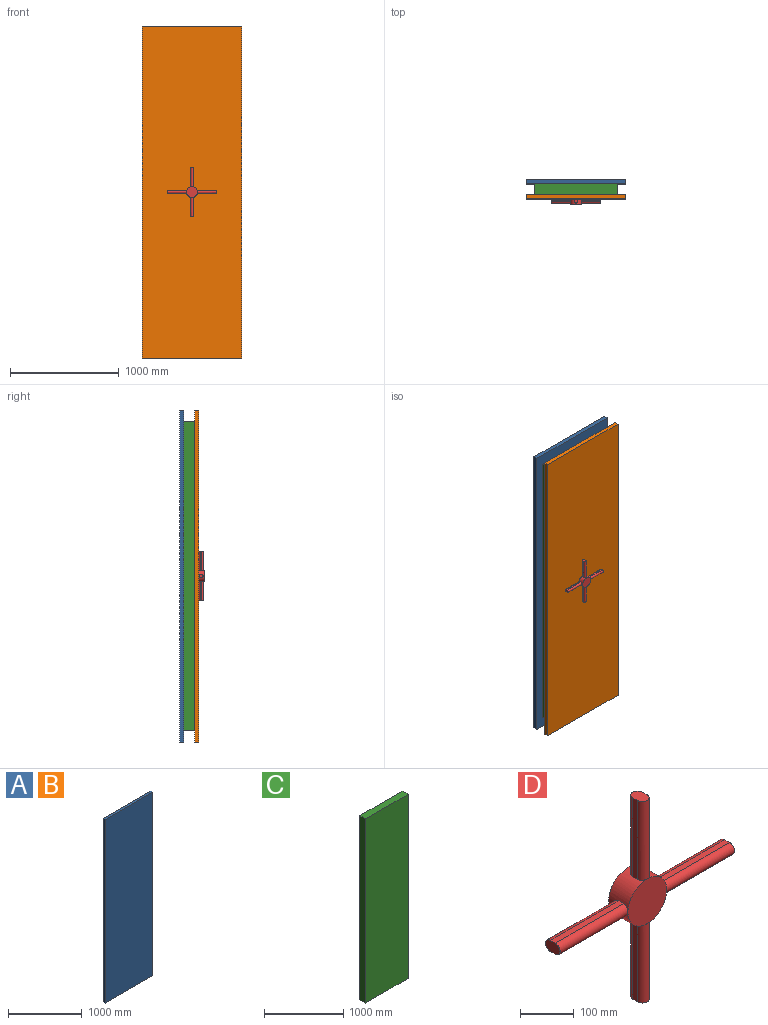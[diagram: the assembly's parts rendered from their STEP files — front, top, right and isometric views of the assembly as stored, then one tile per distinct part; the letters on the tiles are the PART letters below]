
ASSEMBLY  parts=4 mates=3
PART A: 6 faces, bbox 914.4x38.1x3048 mm
  f0: plane 914.4x38.1mm, normal (0,0,-1), area 34838.6mm2, adj f1,f3,f4,f5
  f1: plane 3048x38.1mm, normal (1,0,0), area 116128.8mm2, adj f0,f2,f4,f5
  f2: plane 914.4x38.1mm, normal (0,0,1), area 34838.6mm2, adj f1,f3,f4,f5
  f3: plane 3048x38.1mm, normal (-1,0,0), area 116128.8mm2, adj f0,f2,f4,f5
  f4: plane 3048x914.4mm, normal (0,-1,0), area 2787091.2mm2, adj f0,f1,f2,f3
  f5: plane 3048x914.4mm, normal (0,1,0), area 2787091.2mm2, adj f0,f1,f2,f3
PART B: same geometry as A
PART C: 6 faces, bbox 762x101.6x2844.8 mm
  f0: plane 762x101.6mm, normal (0,0,-1), area 77419.2mm2, adj f1,f3,f4,f5
  f1: plane 2844.8x101.6mm, normal (1,0,0), area 289031.7mm2, adj f0,f2,f4,f5
  f2: plane 762x101.6mm, normal (0,0,1), area 77419.2mm2, adj f1,f3,f4,f5
  f3: plane 2844.8x101.6mm, normal (-1,0,0), area 289031.7mm2, adj f0,f2,f4,f5
  f4: plane 2844.8x762mm, normal (0,-1,0), area 2167737.6mm2, adj f0,f1,f2,f3
  f5: plane 2844.8x762mm, normal (0,1,0), area 2167737.6mm2, adj f0,f1,f2,f3
PART D: 23 faces, bbox 457.2x50.8x457.2 mm
  f0: cylinder r=50.8mm len=101.6mm, axis (0,1,0), area 12867.5mm2, adj f1,f2,f4,f5,f6,f8,f9,f11
  f1: plane 101.6x101.6mm, normal (0,-1,0), area 8107.3mm2, adj f0
  f2: plane 101.6x101.6mm, normal (0,1,0), area 8107.3mm2, adj f0
  f3: plane 38.1x25.4mm, normal (0,0,-1), area 829.3mm2, adj f4,f5,f21,f22
  f4: plane 179.41x12.7mm, normal (1,0,0), area 2278.5mm2, adj f0,f3,f21,f22
  f5: plane 179.41x12.7mm, normal (-1,0,0), area 2278.5mm2, adj f0,f3,f21,f22
  f6: plane 179.41x12.7mm, normal (1,0,0), area 2278.5mm2, adj f0,f7,f17,f18
  f7: plane 38.1x25.4mm, normal (0,0,1), area 829.3mm2, adj f6,f8,f17,f18
  f8: plane 179.41x12.7mm, normal (-1,0,0), area 2278.5mm2, adj f0,f7,f17,f18
  f9: plane 179.41x12.7mm, normal (0,0,-1), area 2278.5mm2, adj f0,f10,f19,f20
  f10: plane 38.1x25.4mm, normal (1,0,0), area 829.3mm2, adj f9,f11,f19,f20
  f11: plane 179.41x12.7mm, normal (0,0,1), area 2278.5mm2, adj f0,f10,f19,f20
  f12: plane 179.41x12.7mm, normal (0,0,-1), area 2278.5mm2, adj f0,f14,f15,f16
  f13: plane 179.41x12.7mm, normal (0,0,1), area 2278.5mm2, adj f0,f14,f15,f16
  f14: plane 38.1x25.4mm, normal (-1,0,0), area 829.3mm2, adj f12,f13,f15,f16
  f15: cylinder r=12.7mm len=179.41mm, axis (1,0,0), area 7126mm2, adj f0,f12,f13,f14
  f16: cylinder r=12.7mm len=179.41mm, axis (-1,0,0), area 7126mm2, adj f0,f12,f13,f14
  f17: cylinder r=12.7mm len=179.41mm, axis (0,0,-1), area 7126mm2, adj f0,f6,f7,f8
  f18: cylinder r=12.7mm len=179.41mm, axis (0,0,1), area 7126mm2, adj f0,f6,f7,f8
  f19: cylinder r=12.7mm len=179.41mm, axis (1,0,0), area 7126mm2, adj f0,f9,f10,f11
  f20: cylinder r=12.7mm len=179.41mm, axis (-1,0,0), area 7126mm2, adj f0,f9,f10,f11
  f21: cylinder r=12.7mm len=179.41mm, axis (0,0,-1), area 7126mm2, adj f0,f3,f4,f5
  f22: cylinder r=12.7mm len=179.41mm, axis (0,0,1), area 7126mm2, adj f0,f3,f4,f5
PLACE A t=(-10.84,-441.12,-140.96)mm
PLACE B rot(axis=(1,0,0),180deg) t=(-10.84,-618.92,-140.96)mm
PLACE C t=(-10.84,-479.22,-140.96)mm
PLACE D rot(axis=(1,0,0),180deg) t=(-10.84,-669.72,-140.96)mm
MATE parallel D.f0 <-> B.f5  axis (0,1,0) through (-10.84,-618.92,-140.96)mm
MATE parallel A.f4 <-> C.f5  axis (0,-1,0) through (-10.84,-479.22,-140.96)mm
MATE parallel B.f4 <-> C.f4  axis (0,1,0) through (-10.84,-580.82,-140.96)mm
